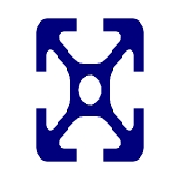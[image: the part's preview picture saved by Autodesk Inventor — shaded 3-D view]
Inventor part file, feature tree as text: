
AUTODESK INVENTOR PART (.ipt)
format: ipt  version: 2020 (Build 240168000, 168)  size: 276,992 bytes
history: native  units: mm
features: other x16, sketch x8, plane x1, split x1
ambient origin geometry x8: Origin, YZ Plane, XZ Plane, XY Plane, X Axis, Y Axis, Z Axis, Center Point
bodies: Body (feature_tree)
feature tree (26):
  other  "Řízená délka"
  other  "Těleso1"
  other  "Start Plane"
  other  "End Plane"
  other  "iFeatureSketch"
  other  "DRAZKA_20:1"
  other  "DRAZKA_20:2"
  other  "DRAZKA_20:3"
  other  "DRAZKA_20:4"
  other  "DIRA_20:1"
  other  "DRAZKA_20:1Axis"
  other  "DRAZKA_20:2Axis"
  other  "DRAZKA_20:3Axis"
  other  "DRAZKA_20:4Axis"
  other  "DIRA_20:1Axis"
  plane  "Work Plane5"
  split  "Split1"
  sketch  "Sketch"  dims[d2=20.0mm d3=20.0mm d4=2.0mm d9=-0.0mm d10=90.0mm d11=0.13mm d12=0.0mm d15=0.83mm d16=0.83mm d17=9.8mm d18=3.0mm d19=4.55mm d20=45.0deg d21=5.2mm d22=1.8mm d24=1.0mm d26=0.83mm d27=0.83mm d28=9.8mm d29=3.0mm d30=4.55mm d31=45.0deg d32=5.2mm d33=1.8mm d35=1.0mm d37=0.83mm d38=0.83mm d39=9.8mm d40=3.0mm d41=4.55mm d42=45.0deg d43=5.2mm d44=1.8mm d46=1.0mm d48=0.83mm d49=0.83mm d50=9.8mm d51=3.0mm d52=4.55mm d53=45.0deg d54=5.2mm d55=1.8mm d57=1.0mm d59=4.3mm d60=0.0mm d61=0.0mm d62=0.0mm d63=0.0mm d64=0.0mm d65=0.0mm d66=0.0mm d67=0.0mm d76=90.0deg d14=90.0mm]
  sketch  "Náčrt11"
  other  "Pracovní rovina4"
  sketch  "Náčrt12"
  sketch  "Náčrt6"
  sketch  "Náčrt7"
  sketch  "Náčrt8"
  sketch  "Náčrt9"
  sketch  "Náčrt10"
